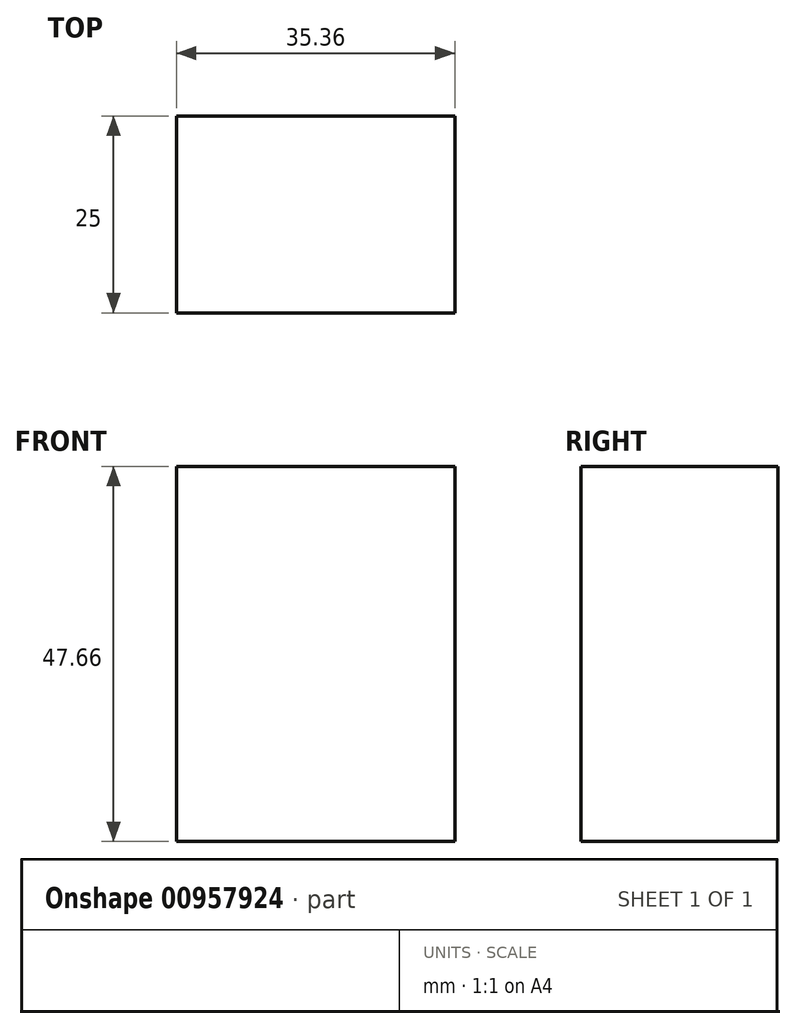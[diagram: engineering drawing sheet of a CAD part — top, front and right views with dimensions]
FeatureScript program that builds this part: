
annotation { "Feature Type Name" : "Feature", "Feature Type Description" : "" }
export const myFeature = defineFeature(function(context is Context, id is Id, definition is map)
    precondition{}
    {
        {
            var Q0;
            Q0=qCreatedBy(makeId("Front.planeOp"),FACE);
            var sketch = newSketch(context, id + "F0", { "sketchPlane" : qUnion([Q0])});
            skLineSegment(sketch, "E0.bottom", {"start": v(-114.7, 13.5) * mm, "end": v(-79.34, 13.5) * mm});
            skLineSegment(sketch, "E0.top", {"start": v(-114.7, -34.16) * mm, "end": v(-79.34, -34.16) * mm});
            skLineSegment(sketch, "E0.left", {"start": v(-114.7, 13.5) * mm, "end": v(-114.7, -34.16) * mm});
            skLineSegment(sketch, "E0.right", {"start": v(-79.34, 13.5) * mm, "end": v(-79.34, -34.16) * mm});
            skSolve(sketch);
        }
        {
            var Q0;
            Q0 = qSketchRegion(id + "F0", true);
            extrude(context, id + "F1", {"entities" : qUnion([Q0]), "depth" : 25 * mm, "offsetDistance" : 25 * mm});
        }
    });
